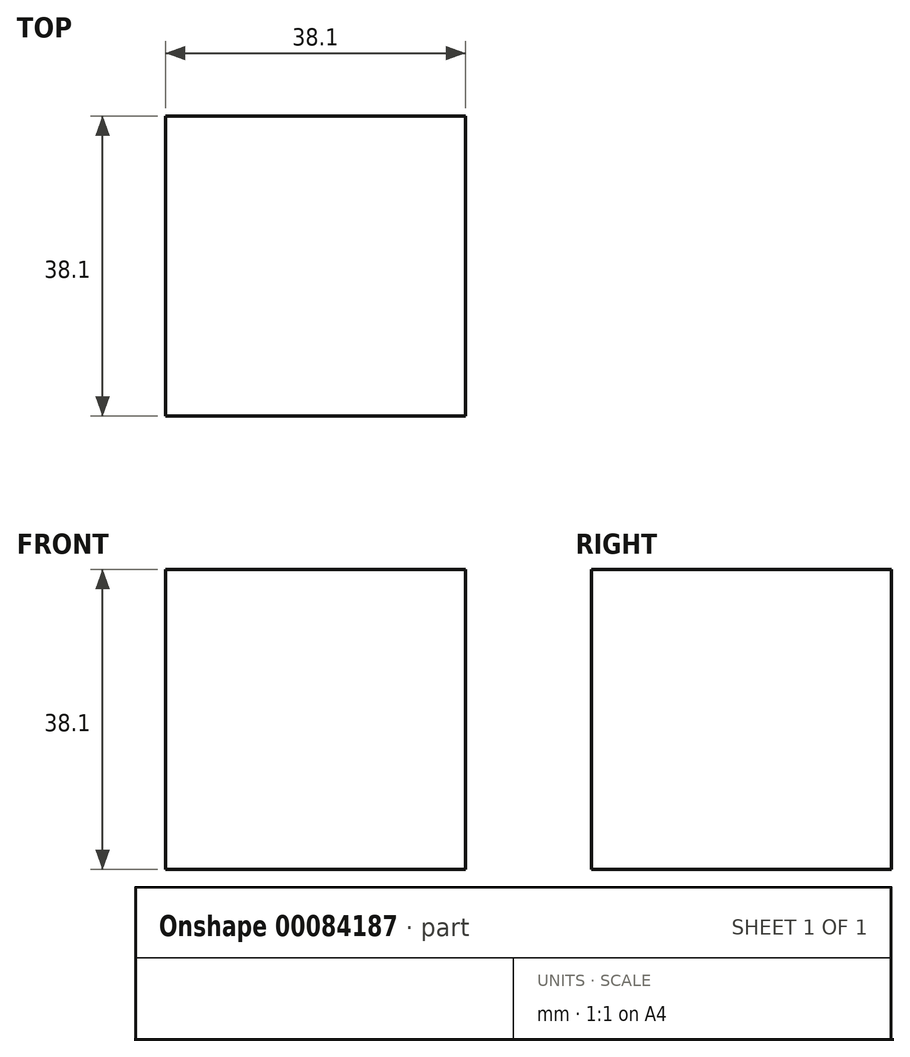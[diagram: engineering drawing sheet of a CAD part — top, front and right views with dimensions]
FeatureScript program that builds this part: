
annotation { "Feature Type Name" : "Feature", "Feature Type Description" : "" }
export const myFeature = defineFeature(function(context is Context, id is Id, definition is map)
    precondition{}
    {
        {
            var Q0;
            Q0=qCreatedBy(makeId("Front.planeOp"),FACE);
            var sketch = newSketch(context, id + "F0", { "sketchPlane" : qUnion([Q0])});
            skLineSegment(sketch, "E0", {"start": v(0, 0) * mm, "end": v(0, 38.1) * mm});
            skLineSegment(sketch, "E1", {"start": v(0, 38.1) * mm, "end": v(38.1, 38.1) * mm});
            skLineSegment(sketch, "E2", {"start": v(38.1, 38.1) * mm, "end": v(38.1, 0) * mm});
            skLineSegment(sketch, "E3", {"start": v(38.1, 0) * mm, "end": v(0, 0) * mm});
            skSolve(sketch);
        }
        {
            var Q0;
            Q0=makeQuery(id+"F0.imprint","IMPRINT",FACE,{"disambiguationData":[TD([[makeQuery(id+"F0.imprint","IMPRINT",EDGE,{"derivedFrom":sQuery(id+"F0.wireOp",EDGE,"E0")}),-1.0]])]});
            extrude(context, id + "F1", {"entities" : qUnion([Q0]), "depth" : 38.1 * mm});
        }
    });
